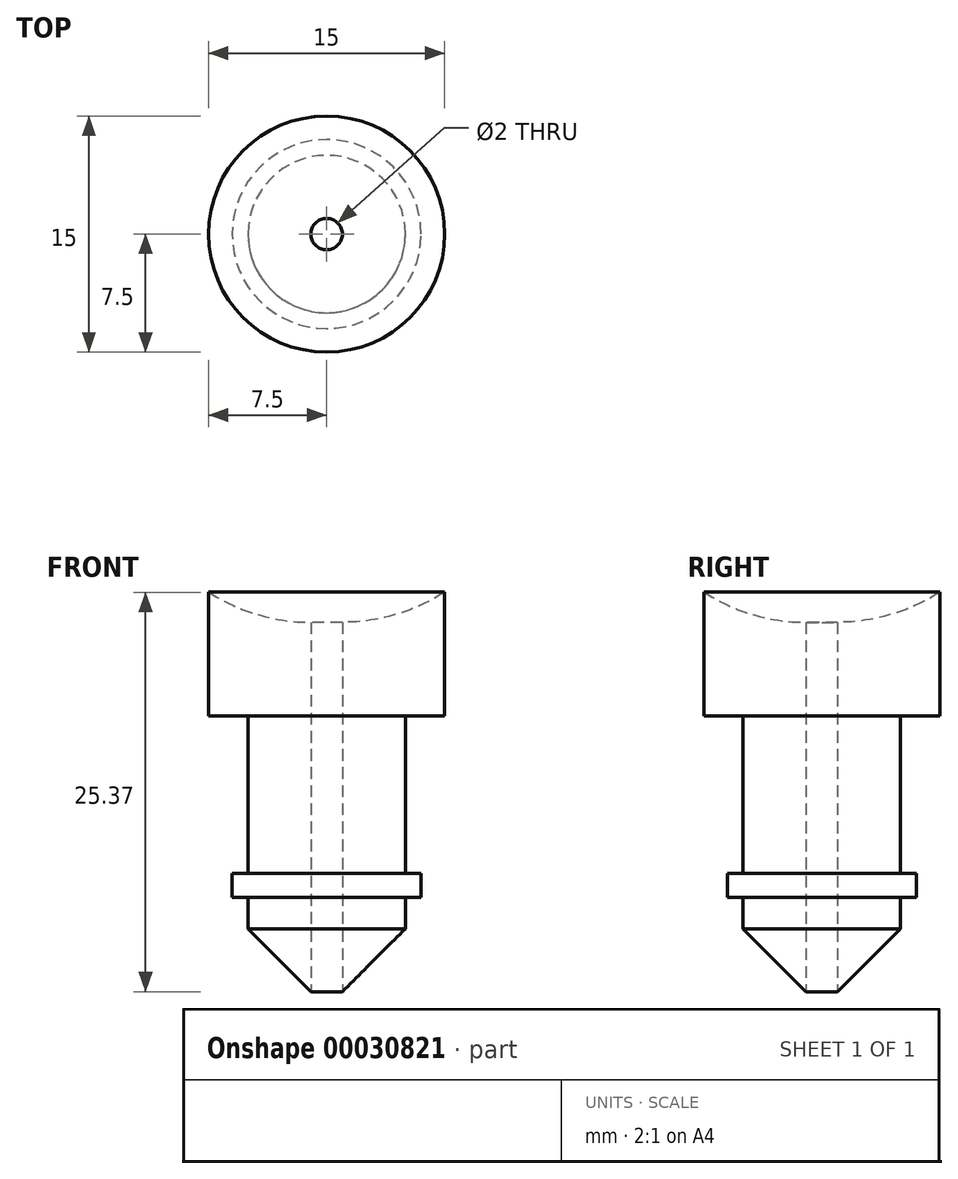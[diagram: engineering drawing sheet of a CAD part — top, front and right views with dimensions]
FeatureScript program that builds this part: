
annotation { "Feature Type Name" : "Feature", "Feature Type Description" : "" }
export const myFeature = defineFeature(function(context is Context, id is Id, definition is map)
    precondition{}
    {
        {
            var Q0;
            Q0=qCreatedBy(makeId("Top.planeOp"),FACE);
            var sketch = newSketch(context, id + "F0", { "sketchPlane" : qUnion([Q0])});
            skCircle(sketch, "E0", {"center": v(0, 0) * mm, "radius": 7.5 * mm});
            skSolve(sketch);
        }
        {
            var Q0;
            Q0 = qSketchRegion(id + "F0", true);
            extrude(context, id + "F1", {"entities" : qUnion([Q0]), "depth" : 10 * mm});
        }
        {
            var Q0;
            Q0=qCreatedBy(makeId("Front.planeOp"),FACE);
            var sketch = newSketch(context, id + "F2", { "sketchPlane" : qUnion([Q0])});
            skLineSegment(sketch, "E1", {"start": v(0, 10) * mm, "end": v(10, 10) * mm});
            skLineSegment(sketch, "E2", {"start": v(0, 10) * mm, "end": v(0, 6) * mm});
            skArc(sketch, "E3", {"start": v(0, 6) * mm, "mid": v(5.47, 6.83) * mm, "end": v(10, 10) * mm});
            skSolve(sketch);
        }
        {
            var Q0;
            Q0 = qSketchRegion(id + "F2", true);
            var Q1;
            Q1=sQuery(id+"F2.wireOp",EDGE,"E2");
            revolve(context, id + "F3", {"operationType" : NewBodyOperationType.REMOVE, "entities" : qUnion([Q0]), "axis" : qUnion([Q1]), "revolveType" : RevolveType.FULL, "oppositeDirection" : true});
        }
        {
            var Q0;
            Q0=makeQuery(id+"F1.opExtrude","CAP_FACE",FACE,{"disambiguationData":[OSD([sQuery(id+"F0.wireOp",EDGE,"E0")])],"isStart":true});
            var sketch = newSketch(context, id + "F4", { "sketchPlane" : qUnion([Q0])});
            skCircle(sketch, "E4", {"center": v(0, 0) * mm, "radius": 5 * mm});
            skSolve(sketch);
        }
        {
            var Q0;
            Q0 = qSketchRegion(id + "F4", true);
            extrude(context, id + "F5", {"entities" : qUnion([Q0]), "operationType" : NewBodyOperationType.ADD, "depth" : 18 * mm});
        }
        {
            var Q0;
            Q0=makeQuery(id+"F5.opExtrude","CAP_FACE",FACE,{"disambiguationData":[OSD([sQuery(id+"F4.wireOp",EDGE,"E4")])],"isStart":false});
            var sketch = newSketch(context, id + "F6", { "sketchPlane" : qUnion([Q0])});
            skCircle(sketch, "E5", {"center": v(0, 0) * mm, "radius": 1 * mm});
            skSolve(sketch);
        }
        {
            var Q0;
            Q0 = qSketchRegion(id + "F6", true);
            extrude(context, id + "F7", {"entities" : qUnion([Q0]), "operationType" : NewBodyOperationType.REMOVE, "endBound" : BoundingType.THROUGH_ALL, "oppositeDirection" : true, "depth" : 25 * mm});
        }
        {
            var Q0;
            Q0=makeQuery(id+"F5.opExtrude","CAP_EDGE",EDGE,{"disambiguationData":[OSD([sQuery(id+"F4.wireOp",EDGE,"E4")])],"isStart":false});
            chamfer(context, id + "F8", {"entities" : qUnion([Q0]), "width" : 4.5 * mm, "tangentPropagation" : true});
        }
        {
            var Q0;
            Q0=qCreatedBy(makeId("Top.planeOp"),FACE);
            cPlane(context, id + "F9", {"entities" : qUnion([Q0]), "cplaneType" : CPlaneType.OFFSET, "offset" : 10 * mm, "oppositeDirection" : true, "width" : 150 * mm, "height" : 150 * mm});
        }
        {
            var Q0;
            Q0=qCreatedBy(id+"F9.planeOp",FACE);
            var sketch = newSketch(context, id + "F10", { "sketchPlane" : qUnion([Q0])});
            skCircle(sketch, "E6", {"center": v(0, 0) * mm, "radius": 6 * mm});
            skCircle(sketch, "E7", {"center": v(0, 0) * mm, "radius": 5 * mm});
            skSolve(sketch);
        }
        {
            var Q0;
            Q0 = qSketchRegion(id + "F10", true);
            extrude(context, id + "F11", {"entities" : qUnion([Q0]), "operationType" : NewBodyOperationType.ADD, "oppositeDirection" : true, "depth" : 1.5 * mm});
        }
    });
